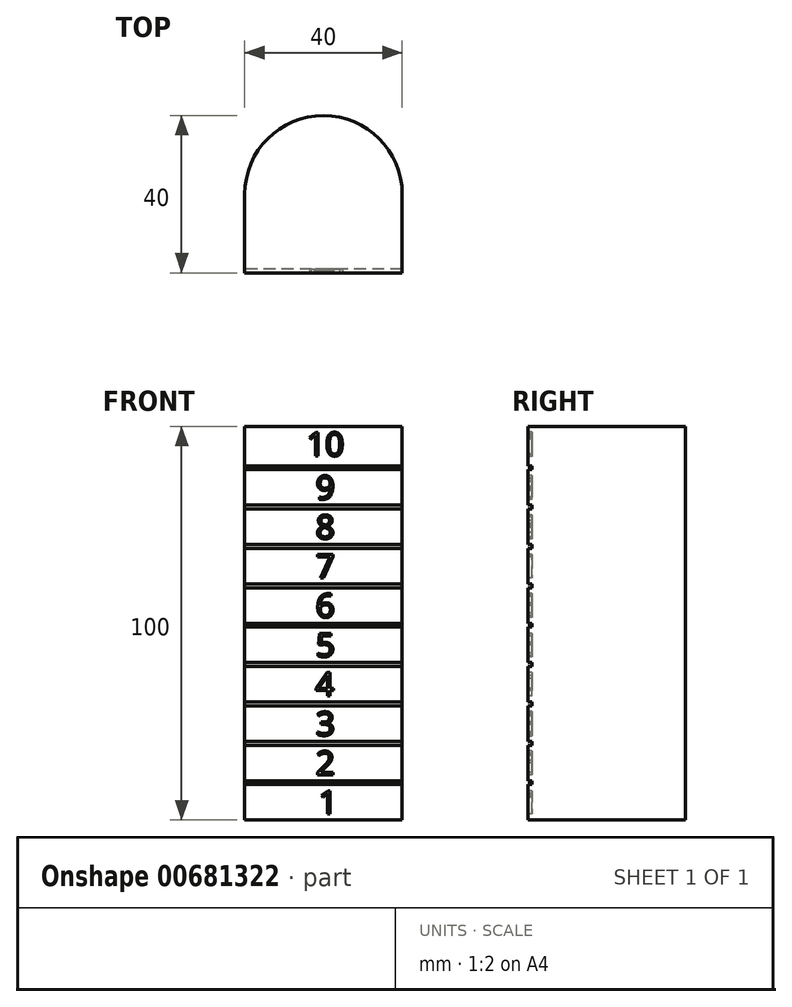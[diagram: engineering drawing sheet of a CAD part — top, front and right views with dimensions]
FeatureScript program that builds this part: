
annotation { "Feature Type Name" : "Feature", "Feature Type Description" : "" }
export const myFeature = defineFeature(function(context is Context, id is Id, definition is map)
    precondition{}
    {
        {
            var Q0;
            Q0=qCreatedBy(makeId("Top.planeOp"),FACE);
            var sketch = newSketch(context, id + "F0", { "sketchPlane" : qUnion([Q0])});
            skLineSegment(sketch, "E0.bottom", {"start": v(0, 0) * mm, "end": v(40, 0) * mm});
            skLineSegment(sketch, "E0.top", {"start": v(0, -20) * mm, "end": v(40, -20) * mm});
            skLineSegment(sketch, "E0.left", {"start": v(0, 0) * mm, "end": v(0, -20) * mm});
            skLineSegment(sketch, "E0.right", {"start": v(40, 0) * mm, "end": v(40, -20) * mm});
            skArc(sketch, "E1", {"start": v(40, 0) * mm, "mid": v(20, 20) * mm, "end": v(0, 0) * mm});
            skSolve(sketch);
        }
        {
            var Q0;
            Q0=makeQuery(id+"F0.imprint","IMPRINT",FACE,{"disambiguationData":[TD([[makeQuery(id+"F0.imprint","IMPRINT",EDGE,{"derivedFrom":sQuery(id+"F0.wireOp",EDGE,"E0.bottom")}),1.0]])]});
            var Q1;
            Q1=makeQuery(id+"F0.imprint","IMPRINT",FACE,{"disambiguationData":[TD([[makeQuery(id+"F0.imprint","IMPRINT",EDGE,{"derivedFrom":sQuery(id+"F0.wireOp",EDGE,"E0.bottom")}),-1.0]])]});
            extrude(context, id + "F1", {"entities" : qUnion([Q0, Q1]), "depth" : 100 * mm, "offsetDistance" : 25 * mm});
        }
        {
            var Q0;
            Q0=makeQuery(id+"F1.opExtrude","SWEPT_FACE",FACE,{"disambiguationData":[OSD([sQuery(id+"F0.wireOp",EDGE,"E0.top")])]});
            var sketch = newSketch(context, id + "F2", { "sketchPlane" : qUnion([Q0])});
            skLineSegment(sketch, "E2.bottom", {"start": v(43, 9) * mm, "end": v(-2, 9) * mm});
            skLineSegment(sketch, "E2.top", {"start": v(43, 10) * mm, "end": v(-2, 10) * mm});
            skLineSegment(sketch, "E2.left", {"start": v(43, 9) * mm, "end": v(43, 10) * mm});
            skLineSegment(sketch, "E2.right", {"start": v(-2, 9) * mm, "end": v(-2, 10) * mm});
            skPoint(sketch, "E2.middle", {"position": v(20.5, 9.5) * mm});
            skLineSegment(sketch, "E3.0.1.0", {"start": v(43, 20) * mm, "end": v(-2, 20) * mm});
            skLineSegment(sketch, "E3.0.1.1", {"start": v(43, 19) * mm, "end": v(-2, 19) * mm});
            skLineSegment(sketch, "E3.0.1.2", {"start": v(-2, 19) * mm, "end": v(-2, 20) * mm});
            skLineSegment(sketch, "E3.0.1.3", {"start": v(43, 19) * mm, "end": v(43, 20) * mm});
            skLineSegment(sketch, "E3.0.2.0", {"start": v(43, 30) * mm, "end": v(-2, 30) * mm});
            skLineSegment(sketch, "E3.0.2.1", {"start": v(43, 29) * mm, "end": v(-2, 29) * mm});
            skLineSegment(sketch, "E3.0.2.2", {"start": v(-2, 29) * mm, "end": v(-2, 30) * mm});
            skLineSegment(sketch, "E3.0.2.3", {"start": v(43, 29) * mm, "end": v(43, 30) * mm});
            skLineSegment(sketch, "E3.0.3.0", {"start": v(43, 40) * mm, "end": v(-2, 40) * mm});
            skLineSegment(sketch, "E3.0.3.1", {"start": v(43, 39) * mm, "end": v(-2, 39) * mm});
            skLineSegment(sketch, "E3.0.3.2", {"start": v(-2, 39) * mm, "end": v(-2, 40) * mm});
            skLineSegment(sketch, "E3.0.3.3", {"start": v(43, 39) * mm, "end": v(43, 40) * mm});
            skLineSegment(sketch, "E3.0.4.0", {"start": v(43, 50) * mm, "end": v(-2, 50) * mm});
            skLineSegment(sketch, "E3.0.4.1", {"start": v(43, 49) * mm, "end": v(-2, 49) * mm});
            skLineSegment(sketch, "E3.0.4.2", {"start": v(-2, 49) * mm, "end": v(-2, 50) * mm});
            skLineSegment(sketch, "E3.0.4.3", {"start": v(43, 49) * mm, "end": v(43, 50) * mm});
            skLineSegment(sketch, "E3.0.5.0", {"start": v(43, 60) * mm, "end": v(-2, 60) * mm});
            skLineSegment(sketch, "E3.0.5.1", {"start": v(43, 59) * mm, "end": v(-2, 59) * mm});
            skLineSegment(sketch, "E3.0.5.2", {"start": v(-2, 59) * mm, "end": v(-2, 60) * mm});
            skLineSegment(sketch, "E3.0.5.3", {"start": v(43, 59) * mm, "end": v(43, 60) * mm});
            skLineSegment(sketch, "E3.0.6.0", {"start": v(43, 70) * mm, "end": v(-2, 70) * mm});
            skLineSegment(sketch, "E3.0.6.1", {"start": v(43, 69) * mm, "end": v(-2, 69) * mm});
            skLineSegment(sketch, "E3.0.6.2", {"start": v(-2, 69) * mm, "end": v(-2, 70) * mm});
            skLineSegment(sketch, "E3.0.6.3", {"start": v(43, 69) * mm, "end": v(43, 70) * mm});
            skLineSegment(sketch, "E3.0.7.0", {"start": v(43, 80) * mm, "end": v(-2, 80) * mm});
            skLineSegment(sketch, "E3.0.7.1", {"start": v(43, 79) * mm, "end": v(-2, 79) * mm});
            skLineSegment(sketch, "E3.0.7.2", {"start": v(-2, 79) * mm, "end": v(-2, 80) * mm});
            skLineSegment(sketch, "E3.0.7.3", {"start": v(43, 79) * mm, "end": v(43, 80) * mm});
            skLineSegment(sketch, "E3.0.8.0", {"start": v(43, 90) * mm, "end": v(-2, 90) * mm});
            skLineSegment(sketch, "E3.0.8.1", {"start": v(43, 89) * mm, "end": v(-2, 89) * mm});
            skLineSegment(sketch, "E3.0.8.2", {"start": v(-2, 89) * mm, "end": v(-2, 90) * mm});
            skLineSegment(sketch, "E3.0.8.3", {"start": v(43, 89) * mm, "end": v(43, 90) * mm});
            skLineSegment(sketch, "E3.direction1", {"start": v(-2, 10) * mm, "end": v(23, 10) * mm, "construction": true});
            skLineSegment(sketch, "E3.direction2", {"start": v(-2, 10) * mm, "end": v(-2, 20) * mm, "construction": true});
            skText(sketch, "E4", { "text": "1", "fontName": "OpenSans-Regular.ttf"});
            skLineSegment(sketch, "E5", {"start": v(20.5, -3.69) * mm, "end": v(20.5, 101) * mm, "construction": true});
            skText(sketch, "E6", { "text": "2", "fontName": "OpenSans-Regular.ttf"});
            skText(sketch, "E7", { "text": "3", "fontName": "OpenSans-Regular.ttf"});
            skText(sketch, "E8", { "text": "4", "fontName": "OpenSans-Regular.ttf"});
            skText(sketch, "E9", { "text": "5", "fontName": "OpenSans-Regular.ttf"});
            skText(sketch, "E10", { "text": "6", "fontName": "OpenSans-Regular.ttf"});
            skText(sketch, "E11", { "text": "7", "fontName": "OpenSans-Regular.ttf"});
            skText(sketch, "E12", { "text": "8", "fontName": "OpenSans-Regular.ttf"});
            skText(sketch, "E13", { "text": "9", "fontName": "OpenSans-Regular.ttf"});
            skText(sketch, "E14", { "text": "10\n", "fontName": "OpenSans-Regular.ttf"});
            const initialGuessF2  = {"E4": [0.01878, 0.0015, 1, 0, 0.006], "E6": [0.01807, 0.0115, 1, 0, 0.006], "E7": [0.0181, 0.0215, 1, 0, 0.006], "E8": [0.01793, 0.0315, 1, 0, 0.006], "E9": [0.01809, 0.0415, 1, 0, 0.006], "E10": [0.01805, 0.0515, 1, 0, 0.006], "E11": [0.01806, 0.0615, 1, 0, 0.006], "E12": [0.01806, 0.0715, 1, 0, 0.006], "E13": [0.01807, 0.0815, 1, 0, 0.006], "E14": [0.01567, 0.0925, 1, 0, 0.006]};
            skSetInitialGuess(sketch, initialGuessF2);
            skSolve(sketch);
        }
        {
            var Q0;
            Q0 = qSketchRegion(id + "F2", true);
            extrude(context, id + "F3", {"entities" : qUnion([Q0]), "operationType" : NewBodyOperationType.REMOVE, "oppositeDirection" : true, "depth" : 1 * mm, "offsetDistance" : 25 * mm});
        }
    });
